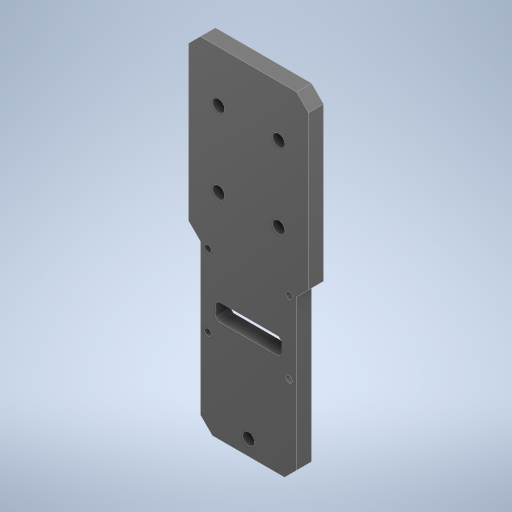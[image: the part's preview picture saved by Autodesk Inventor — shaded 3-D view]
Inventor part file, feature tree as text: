
AUTODESK INVENTOR PART (.ipt)
format: ipt  version: 2024.2 (Build 282272000, 272)  size: 256,000 bytes
history: native  units: in
note: dims shown in document units (in); Inventor stores cm internally (conversion verified against a paired STEP export)
features: extrude x1, chamfer x1, sketch x1, other x1
ambient origin geometry x8: Origin, YZ Plane, XZ Plane, XY Plane, X Axis, Y Axis, Z Axis, Center Point
bodies: Solid1 (feature_tree)
feature tree (4):
  extrude  "Extrusion1"  Depth=0.0787in
  chamfer  "Chamfer1"  Distance=0.2283in
  sketch  "Sketch1"  dims[d0=1.3307in d1=0.4331in d2=0.2283in d3=0.8661in d4=0.3937in d5=0.0in d6=0.0394in d7=0.0787in d8=45.0deg]
  other  "Cortar-Extruir9"
